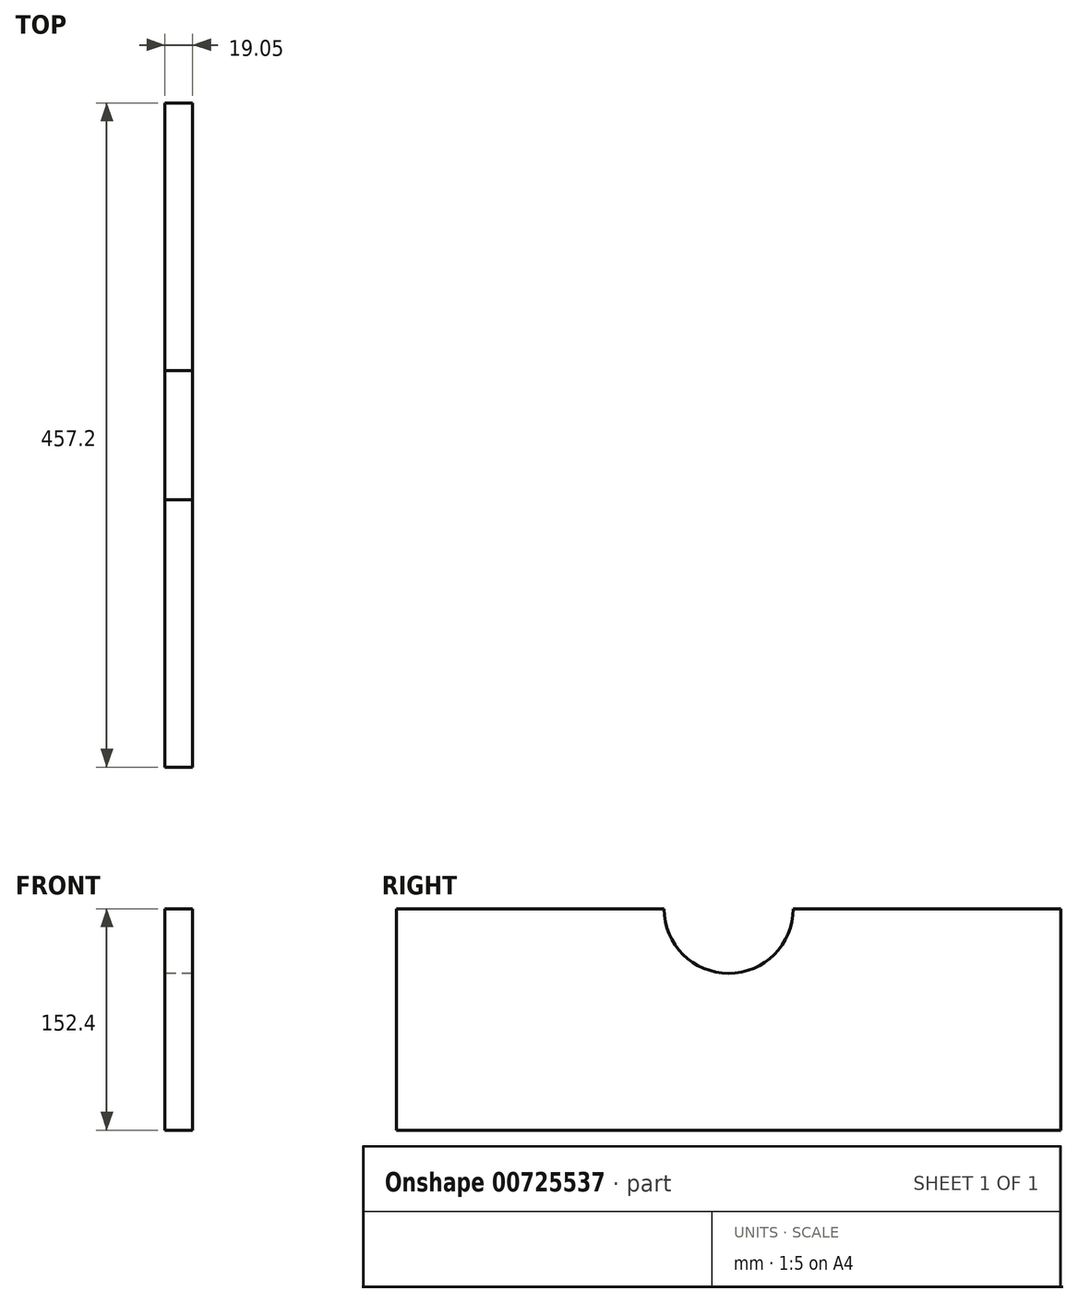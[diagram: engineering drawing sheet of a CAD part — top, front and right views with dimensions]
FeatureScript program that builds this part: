
annotation { "Feature Type Name" : "Feature", "Feature Type Description" : "" }
export const myFeature = defineFeature(function(context is Context, id is Id, definition is map)
    precondition{}
    {
        {
            var Q0;
            Q0=qCreatedBy(makeId("Right.planeOp"),FACE);
            var sketch = newSketch(context, id + "F0", { "sketchPlane" : qUnion([Q0])});
            skLineSegment(sketch, "E0.bottom", {"start": v(228.6, 76.2) * mm, "end": v(-228.6, 76.2) * mm});
            skLineSegment(sketch, "E0.top", {"start": v(228.6, -76.2) * mm, "end": v(-228.6, -76.2) * mm});
            skLineSegment(sketch, "E0.left", {"start": v(228.6, 76.2) * mm, "end": v(228.6, -76.2) * mm});
            skLineSegment(sketch, "E0.right", {"start": v(-228.6, 76.2) * mm, "end": v(-228.6, -76.2) * mm});
            skPoint(sketch, "E0.middle", {"position": v(0, 0) * mm});
            skCircle(sketch, "E1", {"center": v(0, 76.2) * mm, "radius": 44.45 * mm});
            skSolve(sketch);
        }
        {
            var Q0;
            Q0=makeQuery(id+"F0.imprint","IMPRINT",FACE,{"disambiguationData":[TD([[makeQuery(id+"F0.imprint","IMPRINT",EDGE,{"derivedFrom":sQuery(id+"F0.wireOp",EDGE,"E0.top")}),-1.0]])]});
            extrude(context, id + "F1", {"entities" : qUnion([Q0]), "depth" : 19.05 * mm, "offsetDistance" : 25.4 * mm});
        }
    });
